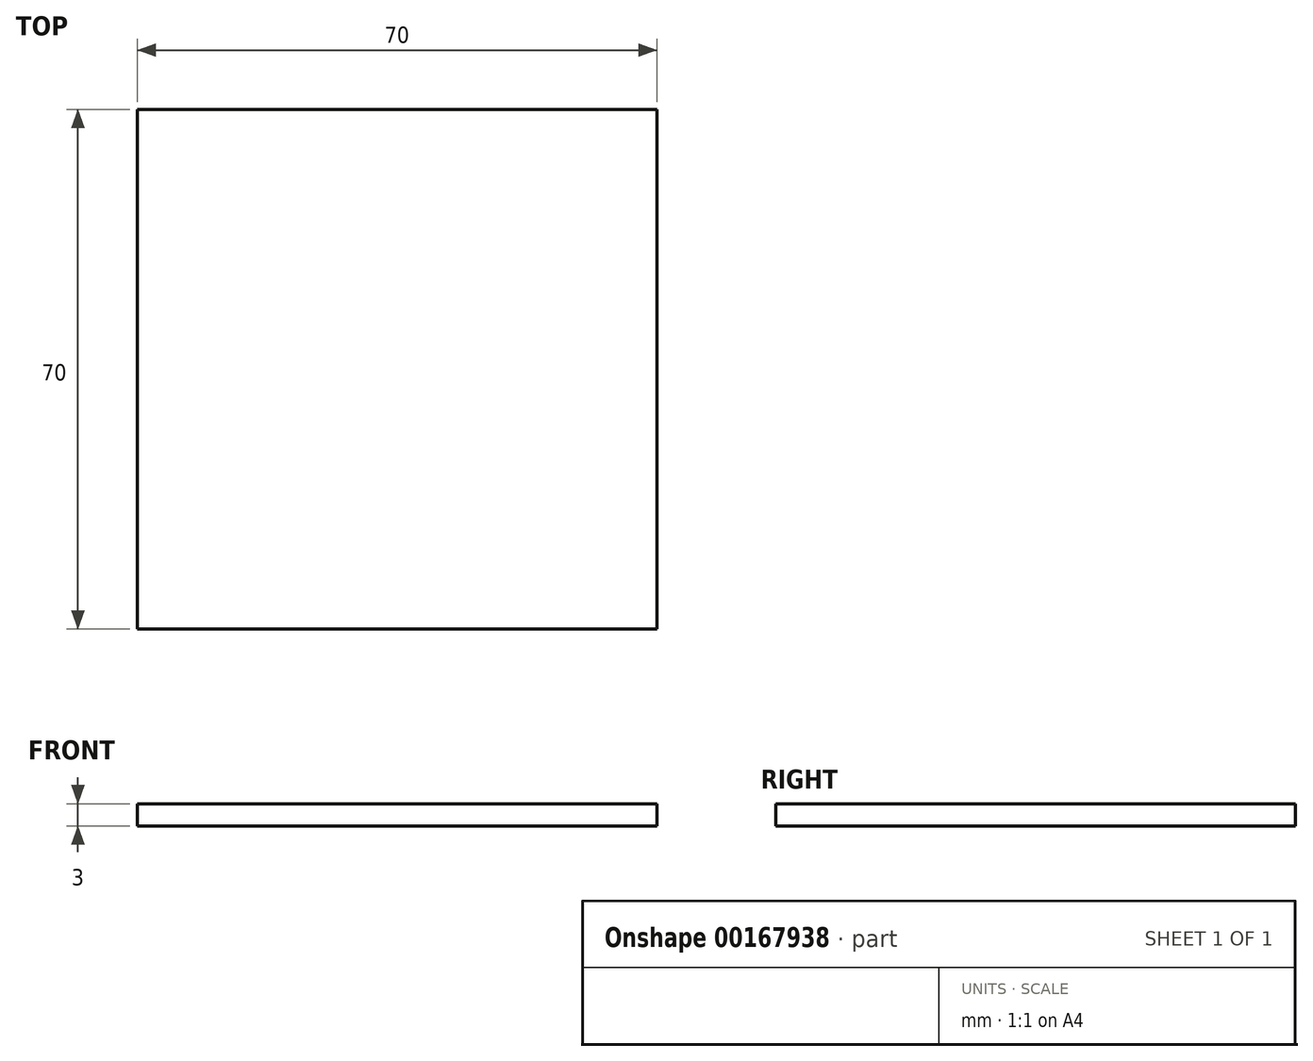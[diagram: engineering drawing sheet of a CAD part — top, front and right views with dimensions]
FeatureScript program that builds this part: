
annotation { "Feature Type Name" : "Feature", "Feature Type Description" : "" }
export const myFeature = defineFeature(function(context is Context, id is Id, definition is map)
    precondition{}
    {
        {
            var Q0;
            Q0=qCreatedBy(makeId("Top.planeOp"),FACE);
            var sketch = newSketch(context, id + "F0", { "sketchPlane" : qUnion([Q0])});
            skLineSegment(sketch, "E0.bottom", {"start": v(0, 0) * mm, "end": v(70, 0) * mm});
            skLineSegment(sketch, "E0.top", {"start": v(0, -70) * mm, "end": v(70, -70) * mm});
            skLineSegment(sketch, "E0.left", {"start": v(0, 0) * mm, "end": v(0, -70) * mm});
            skLineSegment(sketch, "E0.right", {"start": v(70, 0) * mm, "end": v(70, -70) * mm});
            skSolve(sketch);
        }
        {
            var Q0;
            Q0=makeQuery(id+"F0.imprint","IMPRINT",FACE,{"disambiguationData":[TD([[makeQuery(id+"F0.imprint","IMPRINT",EDGE,{"derivedFrom":sQuery(id+"F0.wireOp",EDGE,"E0.bottom")}),-1.0]])]});
            extrude(context, id + "F1", {"entities" : qUnion([Q0]), "depth" : 3 * mm});
        }
    });
